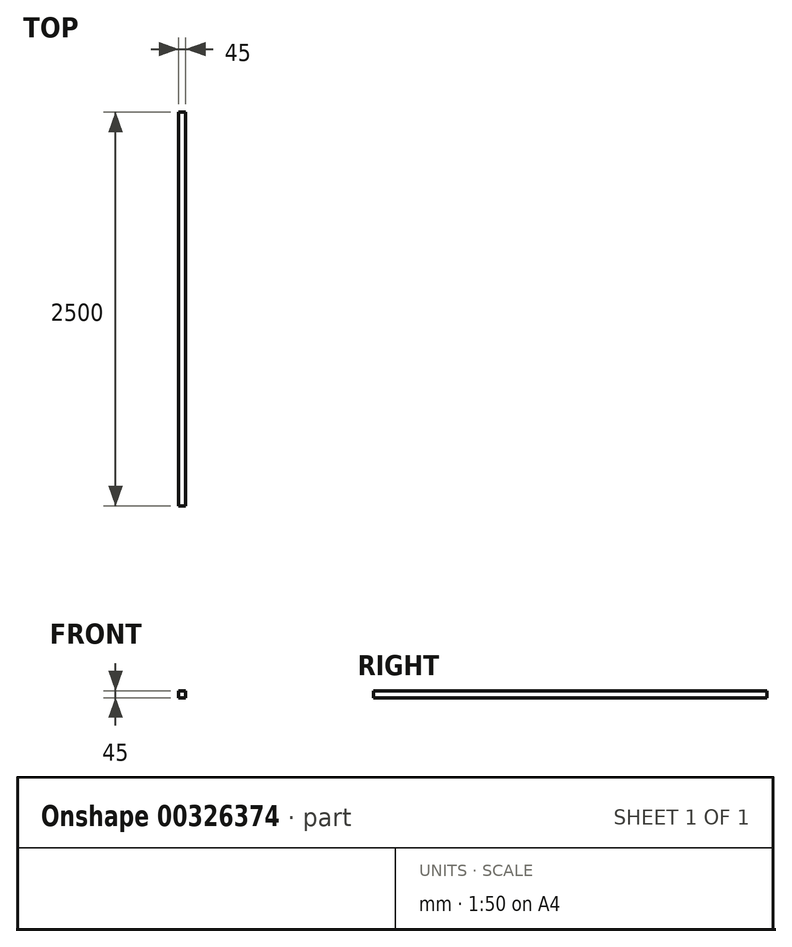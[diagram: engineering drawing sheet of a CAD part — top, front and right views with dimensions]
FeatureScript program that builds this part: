
annotation { "Feature Type Name" : "Feature", "Feature Type Description" : "" }
export const myFeature = defineFeature(function(context is Context, id is Id, definition is map)
    precondition{}
    {
        {
            var Q0;
            Q0=qCreatedBy(makeId("Front.planeOp"),FACE);
            var sketch = newSketch(context, id + "F0", { "sketchPlane" : qUnion([Q0])});
            skLineSegment(sketch, "E0.bottom", {"start": v(0, 0) * mm, "end": v(45, 0) * mm});
            skLineSegment(sketch, "E0.top", {"start": v(0, 45) * mm, "end": v(45, 45) * mm});
            skLineSegment(sketch, "E0.left", {"start": v(0, 0) * mm, "end": v(0, 45) * mm});
            skLineSegment(sketch, "E0.right", {"start": v(45, 0) * mm, "end": v(45, 45) * mm});
            skSolve(sketch);
        }
        {
            var Q0;
            Q0=makeQuery(id+"F0.imprint","IMPRINT",FACE,{"disambiguationData":[TD([[makeQuery(id+"F0.imprint","IMPRINT",EDGE,{"derivedFrom":sQuery(id+"F0.wireOp",EDGE,"E0.bottom")}),1.0]])]});
            extrude(context, id + "F1", {"entities" : qUnion([Q0]), "depth" : 2500 * mm});
        }
    });
